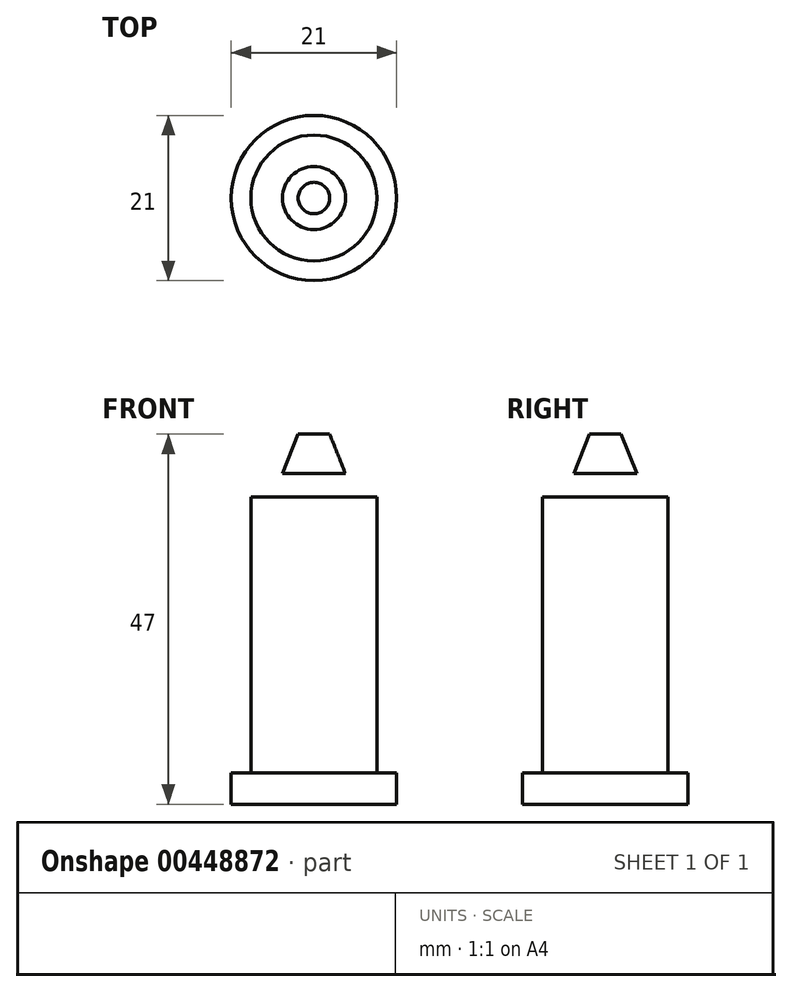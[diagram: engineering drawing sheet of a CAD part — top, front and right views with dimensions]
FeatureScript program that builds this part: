
annotation { "Feature Type Name" : "Feature", "Feature Type Description" : "" }
export const myFeature = defineFeature(function(context is Context, id is Id, definition is map)
    precondition{}
    {
        {
            var Q0;
            Q0=qCreatedBy(makeId("Top.planeOp"),FACE);
            var sketch = newSketch(context, id + "F0", { "sketchPlane" : qUnion([Q0])});
            skCircle(sketch, "E0", {"center": v(0, 0) * mm, "radius": 10.5 * mm});
            skSolve(sketch);
        }
        {
            var Q0;
            Q0=qSketchRegion(id+"F0",true);
            extrude(context, id + "F1", {"entities" : qUnion([Q0]), "depth" : 4 * mm});
        }
        {
            var Q0;
            Q0=qCreatedBy(makeId("Top.planeOp"),FACE);
            var sketch = newSketch(context, id + "F2", { "sketchPlane" : qUnion([Q0])});
            skCircle(sketch, "E1", {"center": v(0, 0) * mm, "radius": 8 * mm});
            skSolve(sketch);
        }
        {
            var Q0;
            Q0=qSketchRegion(id+"F2",true);
            extrude(context, id + "F3", {"entities" : qUnion([Q0]), "operationType" : NewBodyOperationType.ADD, "depth" : 39 * mm});
        }
        {
            var Q0;
            Q0=qCreatedBy(makeId("Right.planeOp"),FACE);
            var sketch = newSketch(context, id + "F4", { "sketchPlane" : qUnion([Q0])});
            skLineSegment(sketch, "E2", {"start": v(0, 44) * mm, "end": v(0, 39) * mm});
            skLineSegment(sketch, "E3", {"start": v(0, 39) * mm, "end": v(5, 39) * mm});
            skArc(sketch, "E4", {"start": v(5, 39) * mm, "mid": v(3.54, 42.54) * mm, "end": v(0, 44) * mm});
            skLineSegment(sketch, "E5", {"start": v(0, 42) * mm, "end": v(4, 42) * mm});
            skLineSegment(sketch, "E6", {"start": v(2, 47) * mm, "end": v(0, 47) * mm});
            skLineSegment(sketch, "E7", {"start": v(0, 47) * mm, "end": v(0, 42) * mm});
            skLineSegment(sketch, "E8", {"start": v(2, 47) * mm, "end": v(4, 42) * mm});
            skSolve(sketch);
        }
        {
            var Q0;
            Q0=makeQuery(id+"F4.imprint","IMPRINT",FACE,{"disambiguationData":[TD([[makeQuery(id+"F4.imprint","IMPRINT",EDGE,{"derivedFrom":sQuery(id+"F4.wireOp",EDGE,"E2")}),1.0]])]});
            var Q1;
            {var subQ4=sQuery(id+"F4.wireOp",EDGE,"E6");Q1=makeQuery(id+"F4.imprint","IMPRINT",FACE,{"disambiguationData":[TD([[makeQuery(id+"F4.imprint","IMPRINT",EDGE,{"derivedFrom":subQ4}),1.0]])]});}
            var Q2;
            {var subQ3=sQuery(id+"F4.wireOp",EDGE,"E5");Q2=makeQuery(id+"F4.imprint","IMPRINT",FACE,{"disambiguationData":[TD([[makeQuery(id+"F4.imprint","IMPRINT",EDGE,{"derivedFrom":subQ3}),1.0]])]});}
            var Q3;
            Q3=sQuery(id+"F4.wireOp",EDGE,"E2");
            revolve(context, id + "F5", {"operationType" : NewBodyOperationType.ADD, "entities" : qUnion([Q0, Q1, Q2]), "axis" : qUnion([Q3]), "revolveType" : RevolveType.FULL});
        }
    });
